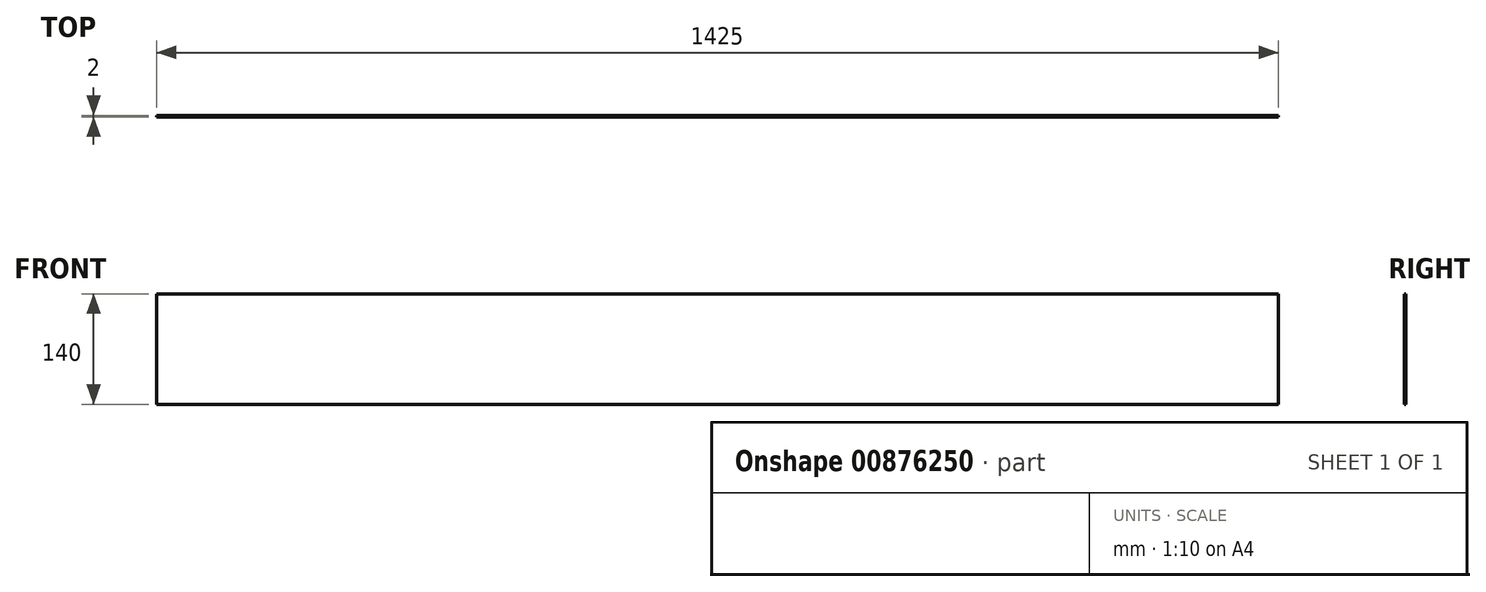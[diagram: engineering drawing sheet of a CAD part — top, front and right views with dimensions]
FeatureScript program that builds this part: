
annotation { "Feature Type Name" : "Feature", "Feature Type Description" : "" }
export const myFeature = defineFeature(function(context is Context, id is Id, definition is map)
    precondition{}
    {
        {
            var Q0;
            Q0=qCreatedBy(makeId("Front.planeOp"),FACE);
            var sketch = newSketch(context, id + "F0", { "sketchPlane" : qUnion([Q0])});
            skLineSegment(sketch, "E0.bottom", {"start": v(0, 0) * mm, "end": v(1425, 0) * mm});
            skLineSegment(sketch, "E0.top", {"start": v(0, -140) * mm, "end": v(1425, -140) * mm});
            skLineSegment(sketch, "E0.left", {"start": v(0, 0) * mm, "end": v(0, -140) * mm});
            skLineSegment(sketch, "E0.right", {"start": v(1425, 0) * mm, "end": v(1425, -140) * mm});
            skSolve(sketch);
        }
        {
            var Q0;
            Q0=makeQuery(id+"F0.imprint","IMPRINT",FACE,{"disambiguationData":[TD([[makeQuery(id+"F0.imprint","IMPRINT",EDGE,{"derivedFrom":sQuery(id+"F0.wireOp",EDGE,"E0.bottom")}),-1.0]])]});
            extrude(context, id + "F1", {"entities" : qUnion([Q0]), "depth" : 2 * mm, "offsetDistance" : 25.4 * mm});
        }
    });
